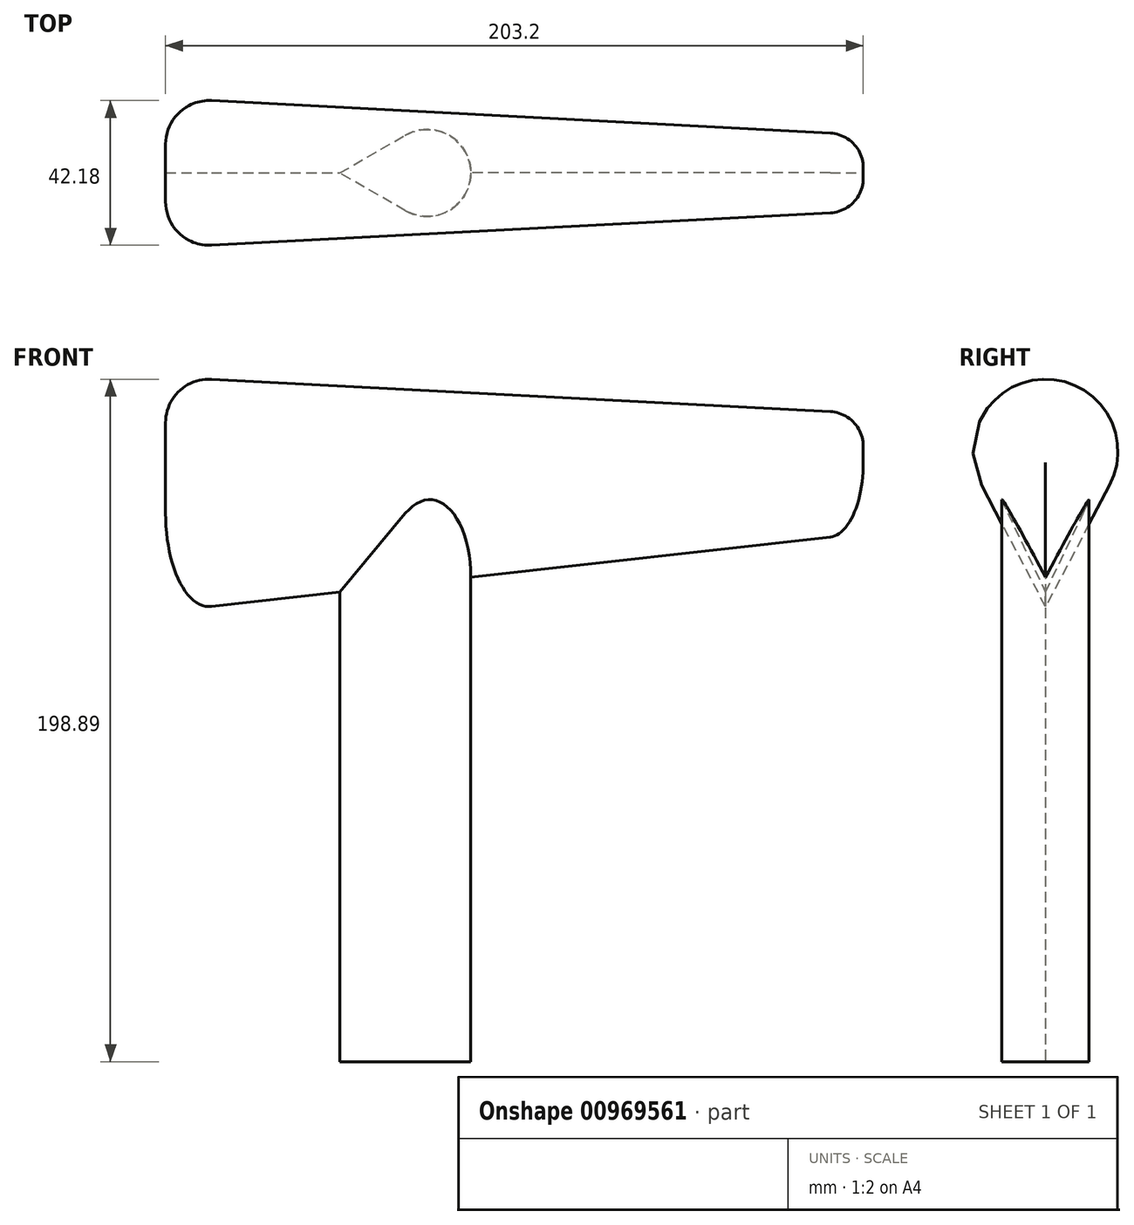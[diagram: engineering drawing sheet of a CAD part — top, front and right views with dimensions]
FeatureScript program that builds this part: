
annotation { "Feature Type Name" : "Feature", "Feature Type Description" : "" }
export const myFeature = defineFeature(function(context is Context, id is Id, definition is map)
    precondition{}
    {
        {
            var Q0;
            Q0=qCreatedBy(makeId("Top.planeOp"),FACE);
            var sketch = newSketch(context, id + "F0", { "sketchPlane" : qUnion([Q0])});
            skArc(sketch, "E0", {"start": v(-6.35, -11) * mm, "mid": v(12.7, 0) * mm, "end": v(-6.35, 11) * mm});
            skLineSegment(sketch, "E1", {"start": v(-6.35, 11) * mm, "end": v(-25.4, 0) * mm});
            skLineSegment(sketch, "E2", {"start": v(-25.4, 0) * mm, "end": v(-6.35, -11) * mm});
            skSolve(sketch);
        }
        {
            var Q0;
            Q0 = qSketchRegion(id + "F0", true);
            extrude(context, id + "F1", {"entities" : qUnion([Q0]), "depth" : 177.8 * mm, "offsetDistance" : 25.4 * mm});
        }
        {
            var Q0;
            Q0=qCreatedBy(makeId("Right.planeOp"),FACE);
            var sketch = newSketch(context, id + "F2", { "sketchPlane" : qUnion([Q0])});
            skArc(sketch, "E3", {"start": v(15.73, 169.5) * mm, "mid": v(0, 195.58) * mm, "end": v(-15.73, 169.5) * mm});
            skLineSegment(sketch, "E4", {"start": v(15.73, 169.5) * mm, "end": v(0, 139.7) * mm});
            skLineSegment(sketch, "E5", {"start": v(0, 139.7) * mm, "end": v(-15.73, 169.5) * mm});
            skSolve(sketch);
        }
        {
            var Q0;
            Q0 = qSketchRegion(id + "F2", true);
            extrude(context, id + "F3", {"entities" : qUnion([Q0]), "operationType" : NewBodyOperationType.ADD, "depth" : 127 * mm, "offsetDistance" : 25.4 * mm, "hasDraft" : true, "draftAngle" : 3 * degree, "draftPullDirection" : true});
        }
        {
            var Q0;
            Q0=makeQuery(id+"F3.opExtrude","CAP_FACE",FACE,{"disambiguationData":[OSD([sQuery(id+"F2.wireOp",EDGE,"E3"),sQuery(id+"F2.wireOp",EDGE,"E4"),sQuery(id+"F2.wireOp",EDGE,"E5")])],"isStart":true});
            var sketch = newSketch(context, id + "F4", { "sketchPlane" : qUnion([Q0])});
            skArc(sketch, "E6.0", {"start": v(-15.73, 169.5) * mm, "mid": v(0, 195.58) * mm, "end": v(15.73, 169.5) * mm});
            skLineSegment(sketch, "E7", {"start": v(15.73, 169.5) * mm, "end": v(0, 139.7) * mm});
            skLineSegment(sketch, "E8", {"start": v(0, 139.7) * mm, "end": v(-15.73, 169.5) * mm});
            skSolve(sketch);
        }
        {
            var Q0;
            Q0 = qSketchRegion(id + "F4", true);
            extrude(context, id + "F5", {"entities" : qUnion([Q0]), "operationType" : NewBodyOperationType.ADD, "depth" : 76.2 * mm, "offsetDistance" : 25.4 * mm, "hasDraft" : true, "draftAngle" : 3 * degree});
        }
        {
            var Q0;
            Q0=makeQuery(id+"F3.opExtrude","CAP_EDGE",EDGE,{"disambiguationData":[OSD([sQuery(id+"F2.wireOp",EDGE,"E3")])],"isStart":false});
            fillet(context, id + "F6", {"entities" : qUnion([Q0]), "radius" : 10.16 * mm, "tangentPropagation" : true, "allowEdgeOverflow" : false});
        }
        {
            var Q0;
            Q0=makeQuery(id+"F5.opExtrude","CAP_EDGE",EDGE,{"disambiguationData":[OSD([sQuery(id+"F4.wireOp",EDGE,"E6.0")])],"isStart":false});
            fillet(context, id + "F7", {"entities" : qUnion([Q0]), "radius" : 12.7 * mm, "tangentPropagation" : true, "allowEdgeOverflow" : false});
        }
    });
